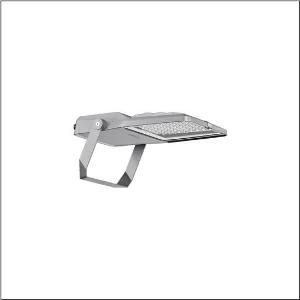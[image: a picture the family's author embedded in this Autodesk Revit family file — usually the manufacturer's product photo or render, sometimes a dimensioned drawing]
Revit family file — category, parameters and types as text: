
# Revit family: floodlight_fl_21_iq_mini___pl33t_5xa7772c3f1a_d349
name_source: partatom
category: Lighting Fixtures
units: mm (PartAtom-declared; Revit-internal decimal feet)

## family parameters
Cut with Voids When Loaded = No
Host = Face
Light Source = No
Part Type = Normal
Room Calculation Point = No
Round Connector Dimension = Use Diameter
Shared = No

## types (1)
- --- (1 x LED, 10390 lm, 87.2 W, 3000K)
    Apparent Load = 87 VA
    CIE Flux Codes = 26 75 99 100 100
    Color Rendering = 80
    Color Temperature = 3000K
    Default Elevation = 1800 mm
    Description = Floodlight FL 21 iQ mini, floodlight, primary light control with lens, of PMMA, primary optical cover: protective disc, of toughened safety glass, transparent, light distribution: PL33T, light emission: direct distribution, installation type: surface-mounted, LED, High Power LED, rated luminous flux: 10.390lm, luminous efficacy: 119lm/W, light colour: 830, colour temperature: 3000K, control: Street-Remote, Auto-Match, Temp-Guard, Night-Set, Smart-Wire, Desk-Remote (wireless, voltage-free reading and setting of iQ features in the workshop via application-optimized NFC function/RFID function), optimised constant luminous flux control (CLO 2.0), with terminal, 6-pole, mains connection: 220..240V, AC, 50/60Hz, start of lifetime: 87W, end of service life: 92W, reduction: 40W, luminaire housing, of diecast aluminium, powder-coated, Siteco® metallic grey (DB 702S), corrosivity category C5 mid according to DIN EN ISO 12944, sealing non-destructively replaceable, mounting bracket, of steel, galvanised, powder-coated, Siteco® metallic grey (DB 702S), protection rating (complete): IP66, insulation class (complete): insulation class II (safety insulation), certification: CE, ENEC, VDE, protection symbol: D, impact resistance: IK08, permissible operating ambient temperature: -40..+40°C, permissible operating ambient temperature for outdoor applications: -40..+50°C, standard: DIN EN 12944, LABS conformity tested according to VDMA 24364:2018-05, packaging unit: 1 piece

Light Distribution: PL33T
    Height = 70 mm
    Lamp = 1 x LED
    Lamp Light Flux = 10390 lm
    Lamp Power = 87.2 W
    Lamp count = 1
    Length = 485 mm
    Luminous efficacy = 119 lm/W
    Manufacturer = Siteco
    ModVariant = No
    Model = 5XA7772C3F1A
    Number of Poles = 1
    OnlyDefault = Yes
    Power Factor = 1
    Product Name = Floodlight FL 21 iQ mini | PL33T
    Product group = floodlight | pylon annexe
    ProductGroupID = 6200
    Protection Class = Protection class II
    Protection Degree = IP 66
    RLX_Detail_Level = 1
    RLX_Emergency_Light_Flux = 0 lm
    RLX_Emergency_Type = 0
    RLX_Emergency_Type_DB = No
    RlxData = <blob elided: 96073 chars, md5=e90d19bc>
    Socket = socket
    Standby Power = 0 W
    System Light Flux = 10390 lm
    System Power = 87 W
    Type Comments = factory setting: luminous flux: 100 % | dim-lin: 254 | 456 mA
    Type Image = l_1006845.jpg
    URL = http://relux.com
    VarID = @adj_099613
    Voltage = 0 V
    Weight = 0.00 kg
    Width = 337 mm

## geometry (parser evidence)
native form markers: Blend x4, Sweep x12
no freeform markers — native parametric forms only
